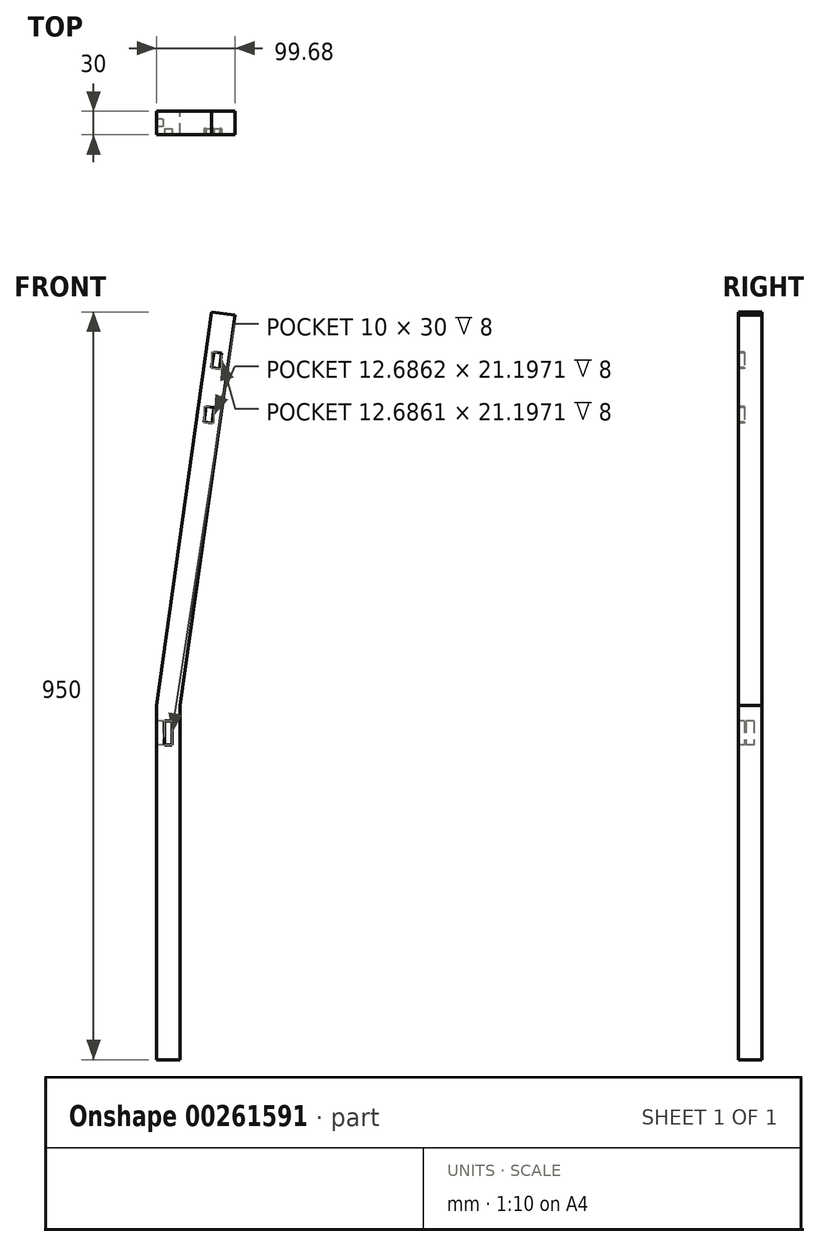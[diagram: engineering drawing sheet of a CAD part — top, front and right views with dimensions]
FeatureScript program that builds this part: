
annotation { "Feature Type Name" : "Feature", "Feature Type Description" : "" }
export const myFeature = defineFeature(function(context is Context, id is Id, definition is map)
    precondition{}
    {
        {
            var Q0;
            Q0=qCreatedBy(makeId("Front.planeOp"),FACE);
            var sketch = newSketch(context, id + "F0", { "sketchPlane" : qUnion([Q0])});
            skLineSegment(sketch, "E0", {"start": v(0, 0) * mm, "end": v(0, -450) * mm});
            skLineSegment(sketch, "E1", {"start": v(0, -450) * mm, "end": v(30, -450) * mm});
            skLineSegment(sketch, "E2", {"start": v(30, -450) * mm, "end": v(30, 0) * mm});
            skLineSegment(sketch, "E3", {"start": v(30, 0) * mm, "end": v(99.68, 495.82) * mm});
            skLineSegment(sketch, "E4", {"start": v(99.68, 495.82) * mm, "end": v(69.98, 500) * mm});
            skLineSegment(sketch, "E5", {"start": v(69.98, 500) * mm, "end": v(0, 0) * mm});
            skSolve(sketch);
        }
        {
            var Q0;
            Q0=qSketchRegion(id+"F0",true);
            extrude(context, id + "F1", {"entities" : qUnion([Q0]), "depth" : 30 * mm});
        }
        {
            var Q0;
            Q0=makeQuery(id+"F1.opExtrude","CAP_FACE",FACE,{"disambiguationData":[OSD([sQuery(id+"F0.wireOp",EDGE,"E0"),sQuery(id+"F0.wireOp",EDGE,"E1"),sQuery(id+"F0.wireOp",EDGE,"E2"),sQuery(id+"F0.wireOp",EDGE,"E3"),sQuery(id+"F0.wireOp",EDGE,"E4"),sQuery(id+"F0.wireOp",EDGE,"E5")])],"isStart":false});
            var sketch = newSketch(context, id + "F2", { "sketchPlane" : qUnion([Q0])});
            skLineSegment(sketch, "E6.bottom", {"start": v(10, -20) * mm, "end": v(20, -20) * mm});
            skLineSegment(sketch, "E6.top", {"start": v(10, -50) * mm, "end": v(20, -50) * mm});
            skLineSegment(sketch, "E6.left", {"start": v(10, -20) * mm, "end": v(10, -50) * mm});
            skLineSegment(sketch, "E6.right", {"start": v(20, -20) * mm, "end": v(20, -50) * mm});
            skSolve(sketch);
        }
        {
            var Q0;
            Q0 = qSketchRegion(id + "F2", true);
            extrude(context, id + "F3", {"entities" : qUnion([Q0]), "operationType" : NewBodyOperationType.REMOVE, "oppositeDirection" : true, "depth" : 8 * mm});
        }
        {
            var Q0;
            Q0=makeQuery(id+"F1.opExtrude","CAP_FACE",FACE,{"disambiguationData":[OSD([sQuery(id+"F0.wireOp",EDGE,"E0"),sQuery(id+"F0.wireOp",EDGE,"E1"),sQuery(id+"F0.wireOp",EDGE,"E2"),sQuery(id+"F0.wireOp",EDGE,"E3"),sQuery(id+"F0.wireOp",EDGE,"E4"),sQuery(id+"F0.wireOp",EDGE,"E5")])],"isStart":false});
            var sketch = newSketch(context, id + "F4", { "sketchPlane" : qUnion([Q0])});
            skLineSegment(sketch, "E7.bottom", {"start": v(72.92, 449.1) * mm, "end": v(82.82, 447.7) * mm});
            skLineSegment(sketch, "E7.top", {"start": v(70.14, 429.29) * mm, "end": v(80.04, 427.9) * mm});
            skLineSegment(sketch, "E7.left", {"start": v(72.92, 449.1) * mm, "end": v(70.14, 429.29) * mm});
            skLineSegment(sketch, "E7.right", {"start": v(82.82, 447.7) * mm, "end": v(80.04, 427.9) * mm});
            skLineSegment(sketch, "E8.bottom", {"start": v(63.18, 379.78) * mm, "end": v(73.08, 378.38) * mm});
            skLineSegment(sketch, "E8.top", {"start": v(60.4, 359.97) * mm, "end": v(70.3, 358.58) * mm});
            skLineSegment(sketch, "E8.left", {"start": v(63.18, 379.78) * mm, "end": v(60.4, 359.97) * mm});
            skLineSegment(sketch, "E8.right", {"start": v(73.08, 378.38) * mm, "end": v(70.3, 358.58) * mm});
            skSolve(sketch);
        }
        {
            var Q0;
            Q0 = qSketchRegion(id + "F4", true);
            extrude(context, id + "F5", {"entities" : qUnion([Q0]), "operationType" : NewBodyOperationType.REMOVE, "oppositeDirection" : true, "depth" : 8 * mm});
        }
        {
            var Q0;
            Q0=makeQuery(id+"F1.opExtrude","SWEPT_FACE",FACE,{"disambiguationData":[OSD([sQuery(id+"F0.wireOp",EDGE,"E0")])]});
            var sketch = newSketch(context, id + "F6", { "sketchPlane" : qUnion([Q0])});
            skLineSegment(sketch, "E9.bottom", {"start": v(10, -20) * mm, "end": v(20, -20) * mm});
            skLineSegment(sketch, "E9.top", {"start": v(10, -50) * mm, "end": v(20, -50) * mm});
            skLineSegment(sketch, "E9.left", {"start": v(10, -20) * mm, "end": v(10, -50) * mm});
            skLineSegment(sketch, "E9.right", {"start": v(20, -20) * mm, "end": v(20, -50) * mm});
            skSolve(sketch);
        }
        {
            var Q0;
            Q0 = qSketchRegion(id + "F6", true);
            extrude(context, id + "F7", {"entities" : qUnion([Q0]), "operationType" : NewBodyOperationType.REMOVE, "oppositeDirection" : true, "depth" : 8 * mm});
        }
    });
